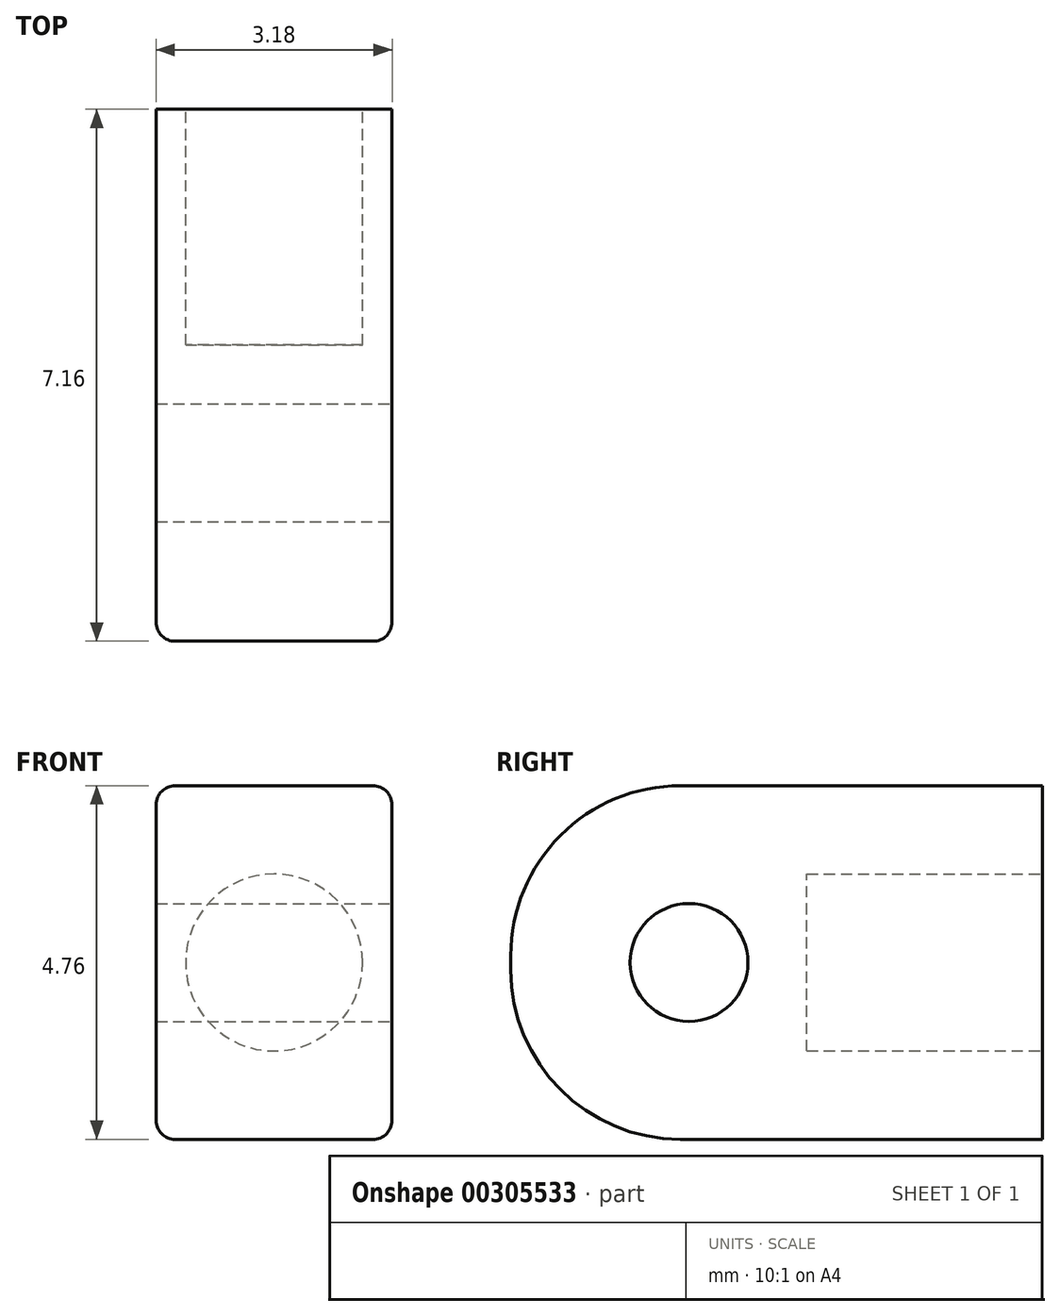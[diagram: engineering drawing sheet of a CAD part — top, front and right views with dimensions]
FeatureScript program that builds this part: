
annotation { "Feature Type Name" : "Feature", "Feature Type Description" : "" }
export const myFeature = defineFeature(function(context is Context, id is Id, definition is map)
    precondition{}
    {
        {
            var Q0;
            Q0=qCreatedBy(makeId("Front.planeOp"),FACE);
            var sketch = newSketch(context, id + "F0", { "sketchPlane" : qUnion([Q0])});
            skLineSegment(sketch, "E0.bottom", {"start": v(-1.59, -2.38) * mm, "end": v(1.59, -2.38) * mm});
            skLineSegment(sketch, "E0.top", {"start": v(-1.59, 2.38) * mm, "end": v(1.59, 2.38) * mm});
            skLineSegment(sketch, "E0.left", {"start": v(-1.59, -2.38) * mm, "end": v(-1.59, 2.38) * mm});
            skLineSegment(sketch, "E0.right", {"start": v(1.59, -2.38) * mm, "end": v(1.59, 2.38) * mm});
            skPoint(sketch, "E0.middle", {"position": v(0, 0) * mm});
            skSolve(sketch);
        }
        {
            var Q0;
            Q0=makeQuery(id+"F0.imprint","IMPRINT",FACE,{"disambiguationData":[TD([[makeQuery(id+"F0.imprint","IMPRINT",EDGE,{"derivedFrom":sQuery(id+"F0.wireOp",EDGE,"E0.bottom")}),1.0]])]});
            extrude(context, id + "F1", {"entities" : qUnion([Q0]), "depth" : 7.16 * mm});
        }
        {
            var Q0;
            Q0=makeQuery(id+"F1.opExtrude","CAP_EDGE",EDGE,{"disambiguationData":[OSD([sQuery(id+"F0.wireOp",EDGE,"E0.top")])],"isStart":false});
            var Q1;
            Q1=makeQuery(id+"F1.opExtrude","CAP_EDGE",EDGE,{"disambiguationData":[OSD([sQuery(id+"F0.wireOp",EDGE,"E0.bottom")])],"isStart":false});
            fillet(context, id + "F2", {"entities" : qUnion([Q0, Q1]), "radius" : 2.3 * mm, "tangentPropagation" : true, "allowEdgeOverflow" : false});
        }
        {
            var Q0;
            Q0=qCreatedBy(makeId("Front.planeOp"),FACE);
            var sketch = newSketch(context, id + "F3", { "sketchPlane" : qUnion([Q0])});
            skCircle(sketch, "E1", {"center": v(0, 0) * mm, "radius": 1.2 * mm});
            skSolve(sketch);
        }
        {
            var Q0;
            Q0 = qSketchRegion(id + "F3", true);
            extrude(context, id + "F4", {"entities" : qUnion([Q0]), "operationType" : NewBodyOperationType.REMOVE, "depth" : 3.17 * mm});
        }
        {
            var Q0;
            Q0=qCreatedBy(makeId("Right.planeOp"),FACE);
            var sketch = newSketch(context, id + "F5", { "sketchPlane" : qUnion([Q0])});
            skLineSegment(sketch, "E2", {"start": v(0, 0) * mm, "end": v(-4.76, 0) * mm, "construction": true});
            skCircle(sketch, "E3", {"center": v(-4.76, 0) * mm, "radius": 0.8 * mm});
            skSolve(sketch);
        }
        {
            var Q0;
            Q0 = qSketchRegion(id + "F5", true);
            extrude(context, id + "F6", {"entities" : qUnion([Q0]), "operationType" : NewBodyOperationType.REMOVE, "oppositeDirection" : true, "depth" : 25.4 * mm, "hasSecondDirection" : true, "secondDirectionOppositeDirection" : false, "secondDirectionDepth" : 25.4 * mm});
        }
        {
            var Q0;
            Q0=makeQuery(id+"F1.opExtrude","SWEPT_EDGE",EDGE,{"disambiguationData":[OSD([sQuery(id+"F0.wireOp",EDGE,"E0.top"),sQuery(id+"F0.wireOp",EDGE,"E0.right")])]});
            var Q1;
            Q1=makeQuery(id+"F2.opFillet","BLEND_EDGE",EDGE,{"blendedFrom":[makeQuery(id+"F1.opExtrude","CAP_EDGE",EDGE,{"disambiguationData":[OSD([sQuery(id+"F0.wireOp",EDGE,"E0.top")])],"isStart":false}),makeQuery(id+"F1.opExtrude","SWEPT_FACE",FACE,{"disambiguationData":[OSD([sQuery(id+"F0.wireOp",EDGE,"E0.right")])]})],"blendedInto":[makeQuery(id+"F1.opExtrude","SWEPT_FACE",FACE,{"disambiguationData":[OSD([sQuery(id+"F0.wireOp",EDGE,"E0.right")])]})]});
            var Q2;
            Q2=makeQuery(id+"F2.opFillet","BLEND_EDGE",EDGE,{"blendedFrom":[makeQuery(id+"F1.opExtrude","CAP_EDGE",EDGE,{"disambiguationData":[OSD([sQuery(id+"F0.wireOp",EDGE,"E0.top")])],"isStart":false}),makeQuery(id+"F1.opExtrude","SWEPT_FACE",FACE,{"disambiguationData":[OSD([sQuery(id+"F0.wireOp",EDGE,"E0.left")])]})],"blendedInto":[makeQuery(id+"F1.opExtrude","SWEPT_FACE",FACE,{"disambiguationData":[OSD([sQuery(id+"F0.wireOp",EDGE,"E0.left")])]})]});
            var Q3;
            Q3=makeQuery(id+"F2.opFillet","BLEND_EDGE",EDGE,{"blendedFrom":[makeQuery(id+"F1.opExtrude","CAP_EDGE",EDGE,{"disambiguationData":[OSD([sQuery(id+"F0.wireOp",EDGE,"E0.bottom")])],"isStart":false}),makeQuery(id+"F1.opExtrude","SWEPT_FACE",FACE,{"disambiguationData":[OSD([sQuery(id+"F0.wireOp",EDGE,"E0.left")])]})],"blendedInto":[makeQuery(id+"F1.opExtrude","SWEPT_FACE",FACE,{"disambiguationData":[OSD([sQuery(id+"F0.wireOp",EDGE,"E0.left")])]})]});
            fillet(context, id + "F7", {"entities" : qUnion([Q0, Q1, Q2, Q3]), "radius" : 0.25 * mm, "tangentPropagation" : true, "allowEdgeOverflow" : false});
        }
    });
